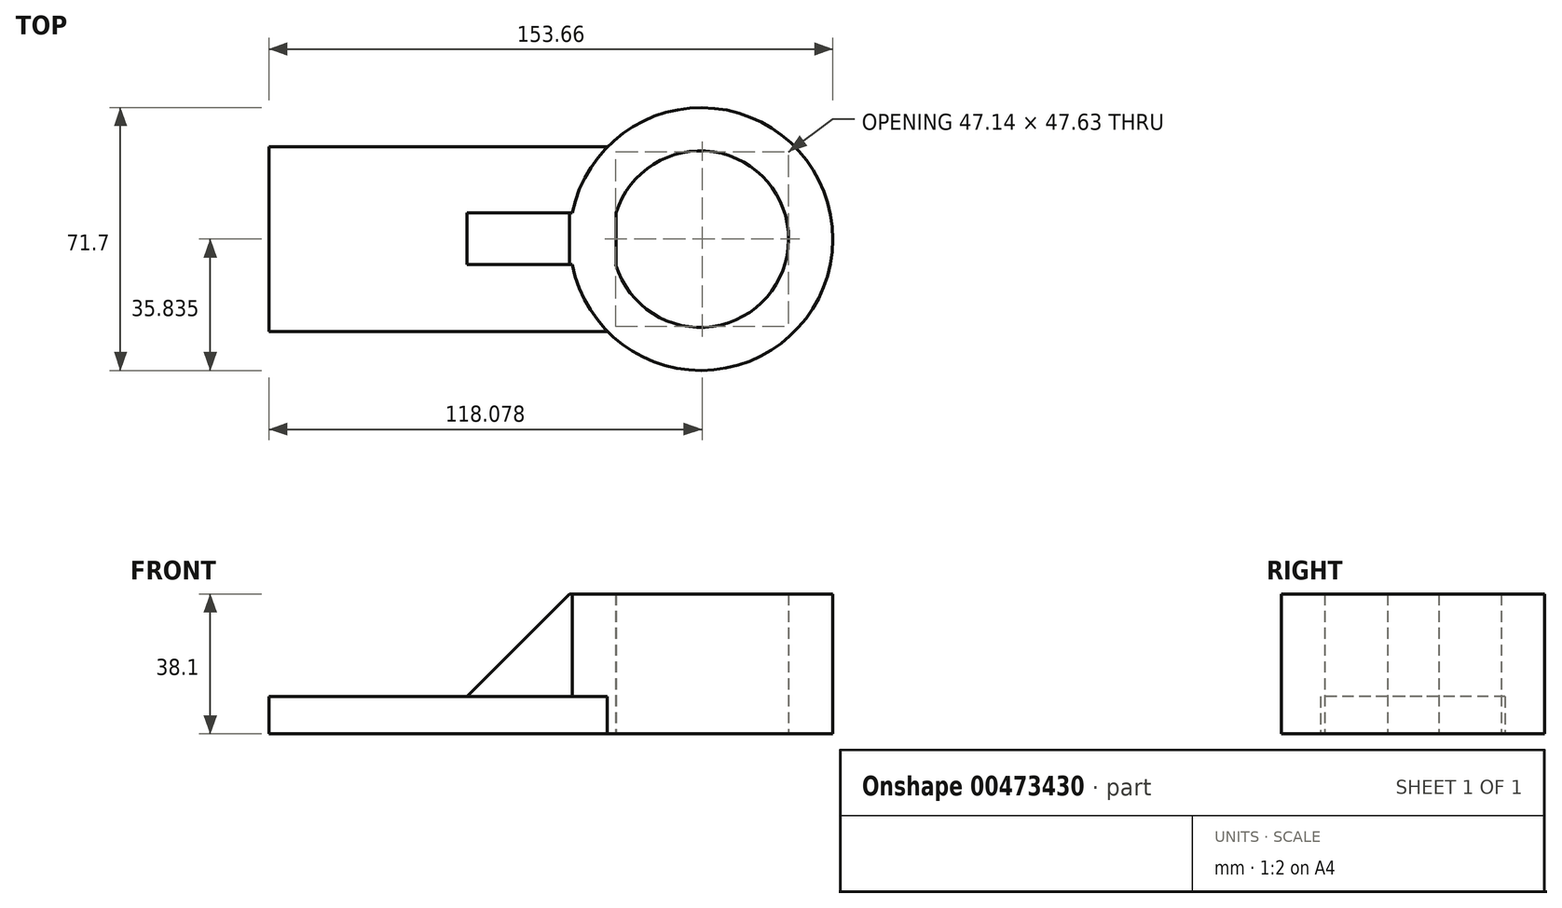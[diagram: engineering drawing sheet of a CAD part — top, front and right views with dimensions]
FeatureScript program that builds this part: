
annotation { "Feature Type Name" : "Feature", "Feature Type Description" : "" }
export const myFeature = defineFeature(function(context is Context, id is Id, definition is map)
    precondition{}
    {
        {
            var Q0;
            Q0=qCreatedBy(makeId("Top.planeOp"),FACE);
            var sketch = newSketch(context, id + "F0", { "sketchPlane" : qUnion([Q0])});
            skCircle(sketch, "E0", {"center": v(46.9, 0) * mm, "radius": 35.85 * mm});
            skLineSegment(sketch, "E1.bottom", {"start": v(21.34, 25.15) * mm, "end": v(-70.92, 25.15) * mm});
            skLineSegment(sketch, "E1.top", {"start": v(21.34, -25.2) * mm, "end": v(-70.92, -25.2) * mm});
            skLineSegment(sketch, "E1.left", {"start": v(21.34, -25.15) * mm, "end": v(21.34, -25.2) * mm});
            skLineSegment(sketch, "E1.right", {"start": v(-70.92, 25.15) * mm, "end": v(-70.92, -25.2) * mm});
            skSolve(sketch);
        }
        {
            var Q0;
            {var subQ0=sQuery(id+"F0.wireOp",EDGE,"E0");var subQ1=makeQuery(id+"F0.imprint","INTERSECT",VERTEX,{"derivedFrom":[subQ0,sQuery(id+"F0.wireOp",EDGE,"E1.bottom")]});Q0=makeQuery(id+"F0.imprint","IMPRINT",FACE,{"disambiguationData":[TD([[makeQuery(id+"F0.imprint","IMPRINT",EDGE,{"disambiguationData":[TD([[subQ1,-1.0]])],"derivedFrom":subQ0}),1.0]])]});}
            var sketch = newSketch(context, id + "F1", { "sketchPlane" : qUnion([Q0])});
            skCircle(sketch, "E2", {"center": v(46.65, 0) * mm, "radius": 24.08 * mm});
            skSolve(sketch);
        }
        {
            var Q0;
            Q0=makeQuery(id+"F1.imprint","IMPRINT",FACE,{"disambiguationData":[TD([[makeQuery(id+"F1.imprint","IMPRINT",EDGE,{"derivedFrom":sQuery(id+"F1.wireOp",EDGE,"E2")}),-1.0]])]});
            extrude(context, id + "F2", {"entities" : qUnion([Q0]), "depth" : 38.1 * mm});
        }
        {
            var Q0;
            {var subQ1=sQuery(id+"F0.wireOp",EDGE,"E1.bottom");Q0=makeQuery(id+"F0.imprint","IMPRINT",FACE,{"disambiguationData":[TD([[makeQuery(id+"F0.imprint","IMPRINT",EDGE,{"derivedFrom":subQ1}),1.0]])]});}
            extrude(context, id + "F3", {"entities" : qUnion([Q0]), "operationType" : NewBodyOperationType.ADD, "depth" : 10.16 * mm});
        }
        {
            var Q0;
            Q0=qCreatedBy(makeId("Top.planeOp"),FACE);
            var sketch = newSketch(context, id + "F4", { "sketchPlane" : qUnion([Q0])});
            skLineSegment(sketch, "E3.bottom", {"start": v(24.18, -6.94) * mm, "end": v(-48.7, -6.94) * mm});
            skLineSegment(sketch, "E3.top", {"start": v(24.18, 7.13) * mm, "end": v(-48.7, 7.13) * mm});
            skLineSegment(sketch, "E3.left", {"start": v(24.18, -6.94) * mm, "end": v(24.18, 7.13) * mm});
            skLineSegment(sketch, "E3.right", {"start": v(-48.7, -6.94) * mm, "end": v(-48.7, 7.13) * mm});
            skSolve(sketch);
        }
        {
            var Q0;
            Q0=makeQuery(id+"F4.imprint","IMPRINT",FACE,{"disambiguationData":[TD([[makeQuery(id+"F4.imprint","IMPRINT",EDGE,{"derivedFrom":sQuery(id+"F4.wireOp",EDGE,"E3.bottom")}),-1.0]])]});
            extrude(context, id + "F5", {"entities" : qUnion([Q0]), "operationType" : NewBodyOperationType.ADD, "depth" : 38.1 * mm});
        }
        {
            var Q0;
            Q0=makeQuery(id+"F5.opExtrude","SWEPT_FACE",FACE,{"disambiguationData":[OSD([sQuery(id+"F4.wireOp",EDGE,"E3.left")])]});
            extrude(context, id + "F6", {"entities" : qUnion([Q0]), "operationType" : NewBodyOperationType.REMOVE, "oppositeDirection" : true, "depth" : 0.5 * mm});
        }
        {
            var Q0;
            Q0=makeQuery(id+"F5.opExtrude","CAP_EDGE",EDGE,{"disambiguationData":[OSD([sQuery(id+"F4.wireOp",EDGE,"E3.right")])],"isStart":false});
            chamfer(context, id + "F7", {"entities" : qUnion([Q0]), "width" : 59.69 * mm, "tangentPropagation" : true});
        }
    });
